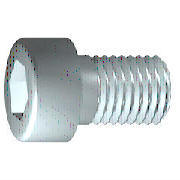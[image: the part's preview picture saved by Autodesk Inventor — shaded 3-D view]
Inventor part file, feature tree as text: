
AUTODESK INVENTOR PART (.ipt)
format: ipt  version: 2024.2 (Build 282272000, 272)  size: 196,096 bytes
history: native  units: mm (DEFAULTED — no unit token found)
features: extrude x1, plane x1, fillet x1, thread x1
ambient origin geometry x7: Origin, YZ Plane, XY Plane, X Axis, Y Axis, Z Axis, Center Point
bodies: Solid1 (feature_tree), Body (feature_tree)
feature tree (4):
  extrude  "Slot"  Depth=8.0mm
  plane  "Work Plane1"
  fillet  "Fillet2"  Radius=0.306825mm
  thread  "Thread2"  [1 undecoded]
note: 1 required parameter value undecoded (feature->parameter linkage not recoverable at this tier; creation-order binding heuristic only, values carry confidence <= 0.55)
